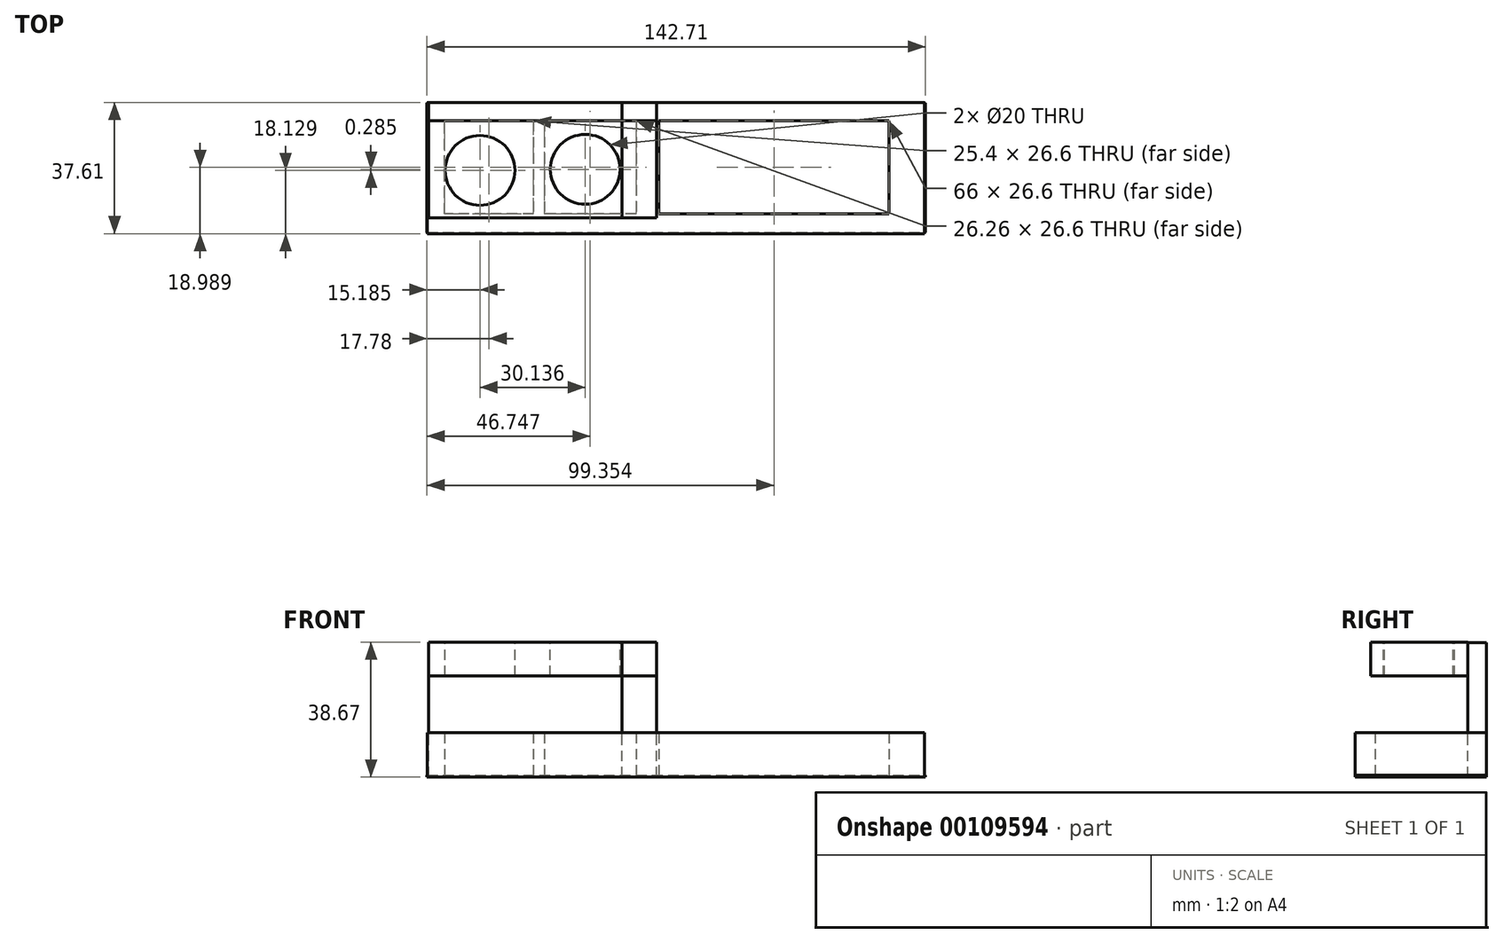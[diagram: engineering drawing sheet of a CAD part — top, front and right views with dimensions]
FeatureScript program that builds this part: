
annotation { "Feature Type Name" : "Feature", "Feature Type Description" : "" }
export const myFeature = defineFeature(function(context is Context, id is Id, definition is map)
    precondition{}
    {
        {
            var Q0;
            Q0=qCreatedBy(makeId("Top.planeOp"),FACE);
            var sketch = newSketch(context, id + "F0", { "sketchPlane" : qUnion([Q0])});
            skLineSegment(sketch, "E0", {"start": v(0, 0) * mm, "end": v(101.6, 0) * mm});
            skLineSegment(sketch, "E1", {"start": v(101.6, 0) * mm, "end": v(101.6, -26.6) * mm});
            skLineSegment(sketch, "E2", {"start": v(101.6, -26.6) * mm, "end": v(0, -26.6) * mm});
            skLineSegment(sketch, "E3", {"start": v(0, -26.6) * mm, "end": v(-50.8, -26.6) * mm});
            skLineSegment(sketch, "E4", {"start": v(-50.8, -26.6) * mm, "end": v(-50.8, 0) * mm});
            skLineSegment(sketch, "E5", {"start": v(-50.8, 0) * mm, "end": v(0, 0) * mm});
            skLineSegment(sketch, "E6", {"start": v(-25.4, 0) * mm, "end": v(-25.4, -26.6) * mm});
            skLineSegment(sketch, "E7", {"start": v(-50.8, -26.6) * mm, "end": v(-55.78, -26.6) * mm});
            skLineSegment(sketch, "E8", {"start": v(-55.78, -26.6) * mm, "end": v(-55.78, 0) * mm});
            skLineSegment(sketch, "E9", {"start": v(-55.78, 0) * mm, "end": v(-50.8, 0) * mm});
            skLineSegment(sketch, "E10", {"start": v(-55.78, -26.6) * mm, "end": v(-55.78, -32.29) * mm});
            skLineSegment(sketch, "E11", {"start": v(-55.78, -32.29) * mm, "end": v(-24.91, -32.29) * mm});
            skLineSegment(sketch, "E12", {"start": v(0, -32.29) * mm, "end": v(-24.91, -32.29) * mm});
            skLineSegment(sketch, "E13", {"start": v(101.6, -32.29) * mm, "end": v(101.6, -26.6) * mm});
            skLineSegment(sketch, "E14", {"start": v(0, -32.29) * mm, "end": v(101.6, -32.29) * mm});
            skLineSegment(sketch, "E15", {"start": v(-55.78, 0) * mm, "end": v(-55.78, 5.32) * mm});
            skLineSegment(sketch, "E16", {"start": v(-55.78, 5.32) * mm, "end": v(101.76, 5.32) * mm});
            skLineSegment(sketch, "E17", {"start": v(101.76, 5.32) * mm, "end": v(101.6, 0) * mm});
            skLineSegment(sketch, "E18", {"start": v(-22.26, 0) * mm, "end": v(-22.26, -26.6) * mm});
            skLineSegment(sketch, "E19", {"start": v(4, 0) * mm, "end": v(4, -26.6) * mm});
            skLineSegment(sketch, "E20", {"start": v(10.47, 0) * mm, "end": v(10.47, -26.6) * mm});
            skLineSegment(sketch, "E21", {"start": v(10.47, -32.29) * mm, "end": v(86.57, -32.29) * mm});
            skLineSegment(sketch, "E22", {"start": v(86.57, -32.29) * mm, "end": v(86.57, 5.32) * mm});
            skLineSegment(sketch, "E23", {"start": v(76.48, -26.6) * mm, "end": v(76.48, 0) * mm});
            skSolve(sketch);
        }
        {
            var Q0;
            Q0=makeQuery(id+"F0.imprint","IMPRINT",FACE,{"disambiguationData":[TD([[makeQuery(id+"F0.imprint","IMPRINT",EDGE,{"derivedFrom":sQuery(id+"F0.wireOp",EDGE,"E4")}),1.0]])]});
            var Q1;
            {var subQ0=sQuery(id+"F0.wireOp",EDGE,"E7");Q1=makeQuery(id+"F0.imprint","IMPRINT",FACE,{"disambiguationData":[TD([[makeQuery(id+"F0.imprint","IMPRINT",EDGE,{"derivedFrom":subQ0}),1.0]])]});}
            var Q2;
            {var subQ5=sQuery(id+"F0.wireOp",EDGE,"E9");Q2=makeQuery(id+"F0.imprint","IMPRINT",FACE,{"disambiguationData":[TD([[makeQuery(id+"F0.imprint","IMPRINT",EDGE,{"derivedFrom":subQ5}),1.0]])]});}
            var Q3;
            {var subQ0=sQuery(id+"F0.wireOp",EDGE,"E6");Q3=makeQuery(id+"F0.imprint","IMPRINT",FACE,{"disambiguationData":[TD([[makeQuery(id+"F0.imprint","IMPRINT",EDGE,{"derivedFrom":subQ0}),1.0]])]});}
            var Q4;
            {var subQ0=sQuery(id+"F0.wireOp",EDGE,"E19");Q4=makeQuery(id+"F0.imprint","IMPRINT",FACE,{"disambiguationData":[TD([[makeQuery(id+"F0.imprint","IMPRINT",EDGE,{"derivedFrom":subQ0}),1.0]])]});}
            var Q5;
            {var subQ0=sQuery(id+"F0.wireOp",EDGE,"E23");Q5=makeQuery(id+"F0.imprint","IMPRINT",FACE,{"disambiguationData":[TD([[makeQuery(id+"F0.imprint","IMPRINT",EDGE,{"derivedFrom":subQ0}),-1.0]])]});}
            extrude(context, id + "F1", {"entities" : qUnion([Q0, Q1, Q2, Q3, Q4, Q5]), "depth" : 12.7 * mm});
        }
        {
            var Q0;
            Q0=qCreatedBy(makeId("Top.planeOp"),FACE);
            var sketch = newSketch(context, id + "F2", { "sketchPlane" : qUnion([Q0])});
            skLineSegment(sketch, "E24.bottom", {"start": v(-55.88, 5.14) * mm, "end": v(101.3, 5.14) * mm});
            skLineSegment(sketch, "E24.top", {"start": v(-55.88, -31.93) * mm, "end": v(101.3, -31.93) * mm});
            skLineSegment(sketch, "E24.left", {"start": v(-55.88, 5.14) * mm, "end": v(-55.88, -31.93) * mm});
            skLineSegment(sketch, "E24.right", {"start": v(101.3, 5.14) * mm, "end": v(101.3, -31.93) * mm});
            skLineSegment(sketch, "E25", {"start": v(86.83, 5.14) * mm, "end": v(86.83, -31.93) * mm});
            skSolve(sketch);
        }
        {
            var Q0;
            {var subQ0=sQuery(id+"F2.wireOp",EDGE,"E24.left");Q0=makeQuery(id+"F2.imprint","IMPRINT",FACE,{"disambiguationData":[TD([[makeQuery(id+"F2.imprint","IMPRINT",EDGE,{"derivedFrom":subQ0}),1.0]])]});}
            extrude(context, id + "F3", {"entities" : qUnion([Q0]), "depth" : 0.5 * mm});
        }
        {
            var Q0;
            Q0=qCreatedBy(makeId("Front.planeOp"),FACE);
            var sketch = newSketch(context, id + "F4", { "sketchPlane" : qUnion([Q0])});
            skLineSegment(sketch, "E26.bottom", {"start": v(0, 0) * mm, "end": v(-55.37, 0) * mm});
            skLineSegment(sketch, "E26.top", {"start": v(0, 57.9) * mm, "end": v(-55.37, 57.9) * mm});
            skLineSegment(sketch, "E26.left", {"start": v(0, 0) * mm, "end": v(0, 57.9) * mm});
            skLineSegment(sketch, "E26.right", {"start": v(-55.37, 0) * mm, "end": v(-55.37, 57.9) * mm});
            skSolve(sketch);
        }
        {
            var Q0;
            Q0=makeQuery(id+"F4.imprint","IMPRINT",FACE,{"disambiguationData":[TD([[makeQuery(id+"F4.imprint","IMPRINT",EDGE,{"derivedFrom":sQuery(id+"F4.wireOp",EDGE,"E26.bottom")}),-1.0]])]});
            var Q1;
            Q1=makeQuery(id+"F1.opExtrude","SWEPT_FACE",FACE,{"disambiguationData":[OSD([sQuery(id+"F0.wireOp",EDGE,"E16")])]});
            extrude(context, id + "F5", {"entities" : qUnion([Q0]), "endBound" : BoundingType.UP_TO_SURFACE, "oppositeDirection" : true, "endBoundEntityFace" : qUnion([Q1]), "depth" : 25.4 * mm});
        }
        {
            var Q0;
            Q0=makeQuery(id+"F5.opExtrude","CAP_FACE",FACE,{"disambiguationData":[OSD([sQuery(id+"F4.wireOp",EDGE,"E26.bottom"),sQuery(id+"F4.wireOp",EDGE,"E26.top"),sQuery(id+"F4.wireOp",EDGE,"E26.left"),sQuery(id+"F4.wireOp",EDGE,"E26.right")])],"isStart":true});
            var sketch = newSketch(context, id + "F6", { "sketchPlane" : qUnion([Q0])});
            skLineSegment(sketch, "E27.bottom", {"start": v(-55.37, 38.67) * mm, "end": v(0, 38.67) * mm});
            skLineSegment(sketch, "E27.top", {"start": v(-55.37, 28.95) * mm, "end": v(0, 28.95) * mm});
            skLineSegment(sketch, "E27.left", {"start": v(-55.37, 38.67) * mm, "end": v(-55.37, 28.95) * mm});
            skLineSegment(sketch, "E27.right", {"start": v(0, 38.67) * mm, "end": v(0, 28.95) * mm});
            skSolve(sketch);
        }
        {
            var Q0;
            Q0=makeQuery(id+"F6.imprint","IMPRINT",FACE,{"disambiguationData":[TD([[makeQuery(id+"F6.imprint","IMPRINT",EDGE,{"derivedFrom":sQuery(id+"F6.wireOp",EDGE,"E27.bottom")}),-1.0]])]});
            extrude(context, id + "F7", {"entities" : qUnion([Q0]), "depth" : 27.75 * mm});
        }
        {
            var Q0;
            Q0=makeQuery(id+"F7.opExtrude","SWEPT_FACE",FACE,{"disambiguationData":[OSD([sQuery(id+"F6.wireOp",EDGE,"E27.bottom")])]});
            var sketch = newSketch(context, id + "F8", { "sketchPlane" : qUnion([Q0])});
            skCircle(sketch, "E28", {"center": v(-40.7, -14.16) * mm, "radius": 10 * mm});
            skLineSegment(sketch, "E29", {"start": v(-55.37, -13.88) * mm, "end": v(0, -13.88) * mm});
            skCircle(sketch, "E30", {"center": v(-10.56, -13.88) * mm, "radius": 10 * mm});
            skSolve(sketch);
        }
        {
            var Q0;
            Q0 = qSketchRegion(id + "F8", true);
            extrude(context, id + "F9", {"entities" : qUnion([Q0]), "operationType" : NewBodyOperationType.REMOVE, "oppositeDirection" : true, "depth" : 10.62 * mm});
        }
        {
            var Q0;
            Q0=makeQuery(id+"F5.opExtrude","SWEPT_FACE",FACE,{"disambiguationData":[OSD([sQuery(id+"F4.wireOp",EDGE,"E26.left")])]});
            extrude(context, id + "F10", {"entities" : qUnion([Q0]), "depth" : 9.88 * mm});
        }
        {
            var Q0;
            Q0=makeQuery(id+"F7.opExtrude","SWEPT_FACE",FACE,{"disambiguationData":[OSD([sQuery(id+"F6.wireOp",EDGE,"E27.right")])]});
            var Q1;
            Q1=makeQuery(id+"F10.opExtrude","CAP_FACE",FACE,{"disambiguationData":[OSD([sQuery(id+"F4.wireOp",EDGE,"E26.left")])],"isStart":false});
            extrude(context, id + "F11", {"entities" : qUnion([Q0]), "endBound" : BoundingType.UP_TO_SURFACE, "endBoundEntityFace" : qUnion([Q1]), "depth" : 8.52 * mm});
        }
        {
            var Q0;
            Q0=makeQuery(id+"F5.opExtrude","SWEPT_FACE",FACE,{"disambiguationData":[OSD([sQuery(id+"F4.wireOp",EDGE,"E26.top")])]});
            var Q1;
            Q1=makeQuery(id+"F10.opExtrude","SWEPT_FACE",FACE,{"disambiguationData":[OSD([sQuery(id+"F4.wireOp",EDGE,"E26.top"),sQuery(id+"F4.wireOp",EDGE,"E26.left")])]});
            extrude(context, id + "F12", {"entities" : qUnion([Q0, Q1]), "operationType" : NewBodyOperationType.REMOVE, "oppositeDirection" : true, "depth" : 19.3 * mm});
        }
    });
